# Revit family: Towel_Ring-Grohe-ATRIO-40307_Series
name_source: partatom
category: Specialty Equipment
units: mm (PartAtom-declared; Revit-internal decimal feet)

## family parameters
Cut with Voids When Loaded = No
Host = Face
OmniClass Number = 23.40.20.21.27
OmniClass Title = Towel Bars
Part Type = Normal
Room Calculation Point = No
Round Connector Dimension = Use Diameter
Shared = Yes

## types (2) — shared parameters
Assembly Code = C1030200
Default Elevation = 1016 mm
Description = Atrio Towel Bar
Height = 212 mm  [stored 0.695538 ft]
Installation Instruction Link = https://americanstandard.box.com
Installation Type = Wall Mounted
Length = 69 mm  [stored 0.226378 ft]
Manufacturer = Grohe
Price = Prices may vary. Please consult Manufacturer Representative for most up-to-date price list.
Product Documentation Link = https://americanstandard.box.com
Product Page URL = https://www.grohe.us
Revised Date = 11/01/2021
URL = https://www.grohe.us
Width = 200 mm  [stored 0.656168 ft]
cUPC Compliant = Yes

## per-type parameters (varying)
| type | Finish | Material | Model |
| 40308003 | Metal-Grohe-003-StarLight Chrome | Metal-Grohe-003-StarLight Chrome | 40307003 |
| 40307EN3 | Metal-Grohe-EN3-Brushed Nickel Infinity Finish | Metal-Grohe-EN3-Brushed Nickel Infinity Finish | 40307EN3 |

note: [stored X ft] marks values corroborated as IEEE doubles in the binary element streams (Revit-internal decimal feet)

## geometry (parser evidence)
native form markers: Sweep x4
no freeform markers — native parametric forms only
